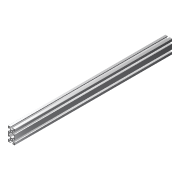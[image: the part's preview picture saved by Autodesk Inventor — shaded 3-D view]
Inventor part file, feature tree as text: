
AUTODESK INVENTOR PART (.ipt)
format: ipt  version: 2018 (Build 220112000, 112)  size: 243,200 bytes
history: native  units: mm
features: extrude x1, sketch x1
ambient origin geometry x8: Origin, YZ Plane, XZ Plane, XY Plane, X Axis, Y Axis, Z Axis, Center Point
bodies: Solid1 (feature_tree)
feature tree (2):
  extrude  "Extrusion1"  [1 undecoded]
  sketch  "Sketch1"  dims[d0=450.0mm d1=0.0mm]
note: 1 required parameter value undecoded (feature->parameter linkage not recoverable at this tier; creation-order binding heuristic only, values carry confidence <= 0.55)
